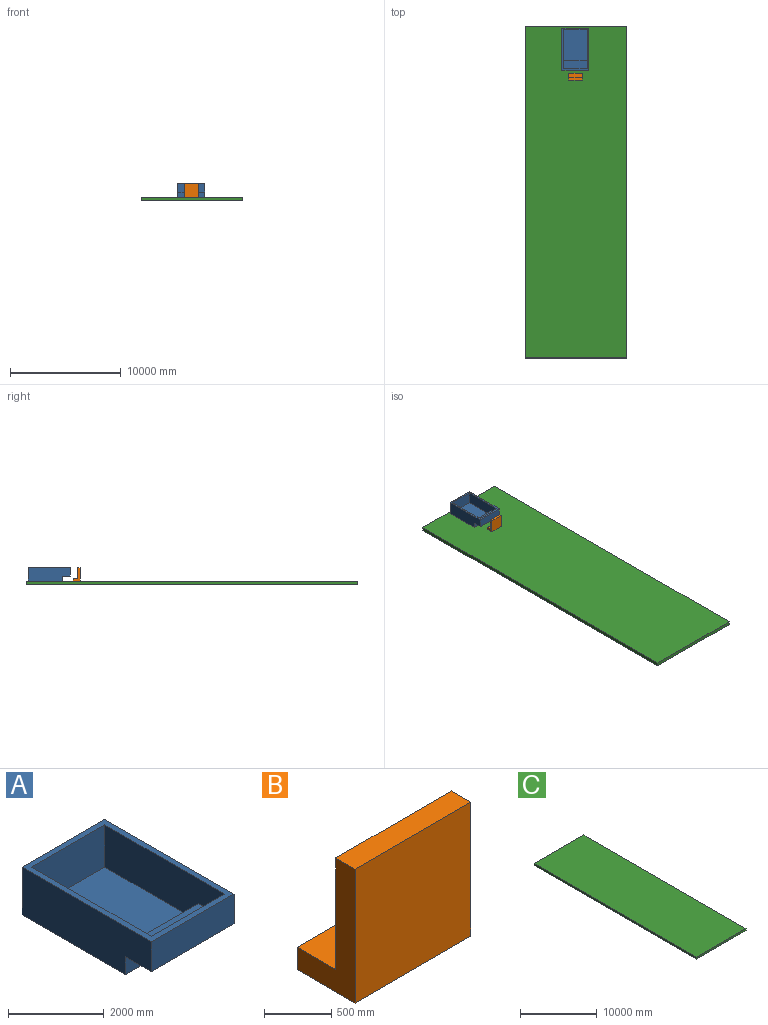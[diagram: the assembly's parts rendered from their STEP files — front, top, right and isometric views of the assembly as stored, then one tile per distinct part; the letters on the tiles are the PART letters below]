
ASSEMBLY  parts=3 mates=2
PART A: 15 faces, bbox 2438.4x3810x1219.2 mm
  f0: plane 3810x2438.4mm, normal (0,0,1), area 1667738.6mm2, adj f4,f5,f6,f7,f11,f12,f13,f14
  f1: plane 2438.4x762mm, normal (0,0,-1), area 1858060.8mm2, adj f2,f5,f6,f7
  f2: plane 2438.4x457.2mm, normal (0,-1,0), area 1114836.5mm2, adj f1,f3,f6,f7
  f3: plane 3048x2438.4mm, normal (0,0,-1), area 7432243.2mm2, adj f2,f4,f6,f7
  f4: plane 2438.4x1219.2mm, normal (0,1,0), area 2972897.3mm2, adj f0,f3,f6,f7
  f5: plane 2438.4x762mm, normal (0,-1,0), area 1858060.8mm2, adj f0,f1,f6,f7
  f6: plane 3810x1219.2mm, normal (1,0,0), area 4296765.6mm2, adj f0,f1,f2,f3,f4,f5
  f7: plane 3810x1219.2mm, normal (-1,0,0), area 4296765.6mm2, adj f0,f1,f2,f3,f4,f5
  f8: plane 2159x762mm, normal (0,0,1), area 1645158mm2, adj f9,f12,f13,f14
  f9: plane 2159x457.2mm, normal (0,1,0), area 987094.8mm2, adj f8,f10,f13,f14
  f10: plane 2768.6x2159mm, normal (0,0,1), area 5977407.4mm2, adj f9,f11,f13,f14
  f11: plane 2159x1079.5mm, normal (0,-1,0), area 2330640.5mm2, adj f0,f10,f13,f14
  f12: plane 2159x622.3mm, normal (0,1,0), area 1343545.7mm2, adj f0,f8,f13,f14
  f13: plane 3530.6x1079.5mm, normal (-1,0,0), area 3462896.3mm2, adj f0,f8,f9,f10,f11,f12
  f14: plane 3530.6x1079.5mm, normal (1,0,0), area 3462896.3mm2, adj f0,f8,f9,f10,f11,f12
PART B: 8 faces, bbox 1219.2x609.6x1219.2 mm
  f0: plane 1219.2x203.2mm, normal (0,1,0), area 247741.4mm2, adj f1,f5,f6,f7
  f1: plane 1219.2x406.4mm, normal (0,0,1), area 495482.9mm2, adj f0,f2,f6,f7
  f2: plane 1219.2x1016mm, normal (0,1,0), area 1238707.2mm2, adj f1,f3,f6,f7
  f3: plane 1219.2x203.2mm, normal (0,0,1), area 247741.4mm2, adj f2,f4,f6,f7
  f4: plane 1219.2x1219.2mm, normal (0,-1,0), area 1486448.6mm2, adj f3,f5,f6,f7
  f5: plane 1219.2x609.6mm, normal (0,0,-1), area 743224.3mm2, adj f0,f4,f6,f7
  f6: plane 1219.2x609.6mm, normal (1,0,0), area 330321.9mm2, adj f0,f1,f2,f3,f4,f5
  f7: plane 1219.2x609.6mm, normal (-1,0,0), area 330321.9mm2, adj f0,f1,f2,f3,f4,f5
PART C: 6 faces, bbox 9144x30000x304.8 mm
  f0: plane 30000x304.8mm, normal (1,0,0), area 9144000mm2, adj f1,f3,f4,f5
  f1: plane 9144x304.8mm, normal (0,1,0), area 2787091.2mm2, adj f0,f2,f4,f5
  f2: plane 30000x304.8mm, normal (-1,0,0), area 9144000mm2, adj f1,f3,f4,f5
  f3: plane 9144x304.8mm, normal (0,-1,0), area 2787091.2mm2, adj f0,f2,f4,f5
  f4: plane 30000x9144mm, normal (0,0,-1), area 274320000mm2, adj f0,f1,f2,f3
  f5: plane 30000x9144mm, normal (0,0,1), area 274320000mm2, adj f0,f1,f2,f3
PLACE A t=(-57.59,11742.26,457.2)mm
PLACE B t=(-40.14,10719.09,203.2)mm
PLACE C at identity fixed
MATE planar B.f5 <-> C.f5  axis (0,0,-1) through (-40.14,10414.29,0)mm
MATE planar A.f3 <-> C.f5  axis (0,0,-1) through (-57.59,13266.26,0)mm
